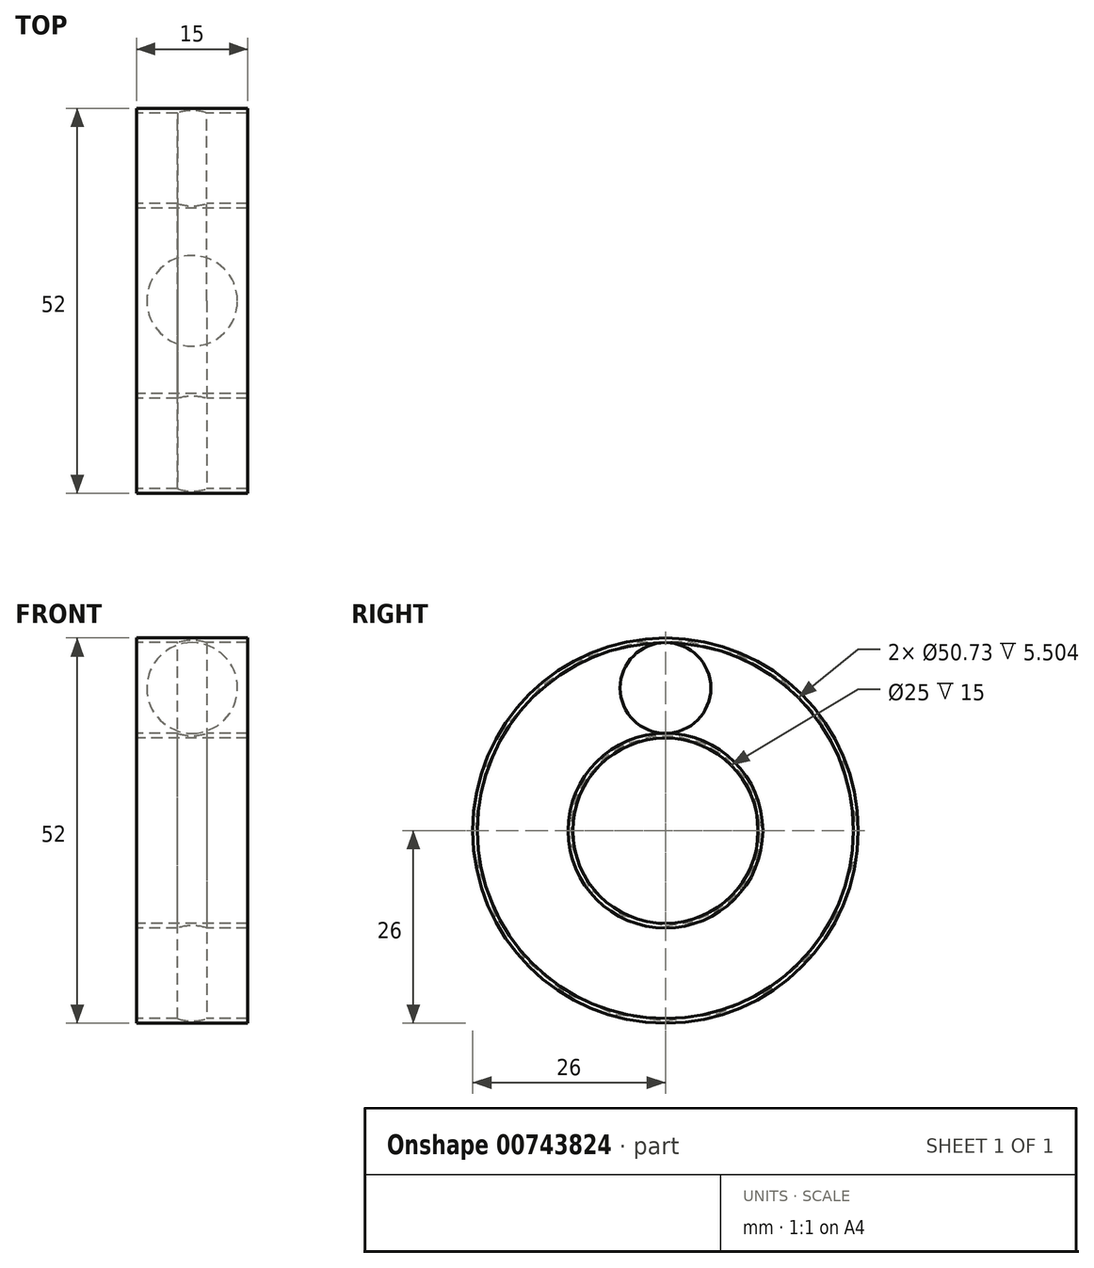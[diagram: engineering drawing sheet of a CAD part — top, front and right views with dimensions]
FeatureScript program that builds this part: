
annotation { "Feature Type Name" : "Feature", "Feature Type Description" : "" }
export const myFeature = defineFeature(function(context is Context, id is Id, definition is map)
    precondition{}
    {
        {
            var Q0;
            Q0=qCreatedBy(makeId("Right.planeOp"),FACE);
            var sketch = newSketch(context, id + "F0", { "sketchPlane" : qUnion([Q0])});
            skCircle(sketch, "E0", {"center": v(0, 0) * mm, "radius": 12.5 * mm});
            skCircle(sketch, "E1", {"center": v(0, 0) * mm, "radius": 13.14 * mm});
            skCircle(sketch, "E2", {"center": v(0, 0) * mm, "radius": 25.37 * mm});
            skCircle(sketch, "E3", {"center": v(0, 0) * mm, "radius": 26 * mm});
            skLineSegment(sketch, "E4", {"start": v(0, 13.14) * mm, "end": v(0, 19.25) * mm});
            skLineSegment(sketch, "E5", {"start": v(0, 19.25) * mm, "end": v(0, 25.37) * mm});
            skCircle(sketch, "E6", {"center": v(0, 19.25) * mm, "radius": 6.11 * mm});
            skSolve(sketch);
        }
        {
            var Q0;
            Q0=makeQuery(id+"F0.imprint","IMPRINT",FACE,{"disambiguationData":[TD([[makeQuery(id+"F0.imprint","IMPRINT",EDGE,{"derivedFrom":sQuery(id+"F0.wireOp",EDGE,"E0")}),-1.0]])]});
            var Q1;
            {var subQ0=sQuery(id+"F0.wireOp",EDGE,"E1");var subQ1=makeQuery(id+"F0.imprint","INTERSECT",VERTEX,{"derivedFrom":[subQ0,sQuery(id+"F0.wireOp",EDGE,"E4")]});Q1=makeQuery(id+"F0.imprint","IMPRINT",FACE,{"disambiguationData":[TD([[makeQuery(id+"F0.imprint","IMPRINT",EDGE,{"disambiguationData":[TD([[subQ1,1.0]])],"derivedFrom":subQ0}),1.0]])]});}
            var Q2;
            Q2=makeQuery(id+"F0.imprint","IMPRINT",FACE,{"disambiguationData":[TD([[makeQuery(id+"F0.imprint","IMPRINT",EDGE,{"derivedFrom":sQuery(id+"F0.wireOp",EDGE,"E3")}),1.0]])]});
            var Q3;
            {var subQ0=sQuery(id+"F0.wireOp",EDGE,"E2");var subQ1=makeQuery(id+"F0.imprint","INTERSECT",VERTEX,{"derivedFrom":[subQ0,sQuery(id+"F0.wireOp",EDGE,"E5")]});Q3=makeQuery(id+"F0.imprint","IMPRINT",FACE,{"disambiguationData":[TD([[makeQuery(id+"F0.imprint","IMPRINT",EDGE,{"disambiguationData":[TD([[subQ1,1.0]])],"derivedFrom":subQ0}),-1.0]])]});}
            extrude(context, id + "F1", {"entities" : qUnion([Q0, Q1, Q2, Q3]), "endBound" : BoundingType.SYMMETRIC, "depth" : 15 * mm, "offsetDistance" : 25.4 * mm});
        }
        {
            var Q0;
            Q0=qCreatedBy(makeId("Front.planeOp"),FACE);
            var sketch = newSketch(context, id + "F2", { "sketchPlane" : qUnion([Q0])});
            skPoint(sketch, "E7", {"position": v(0, 19.25) * mm});
            skCircle(sketch, "E8", {"center": v(0, 19.25) * mm, "radius": 6.43 * mm});
            skSolve(sketch);
        }
        {
            var Q0;
            Q0=makeQuery(id+"F2.imprint","IMPRINT",FACE,{"disambiguationData":[TD([[makeQuery(id+"F2.imprint","IMPRINT",EDGE,{"derivedFrom":sQuery(id+"F2.wireOp",EDGE,"E8")}),1.0]])]});
            var Q1;
            Q1=makeQuery(id+"F1.opExtrude","SWEPT_FACE",FACE,{"disambiguationData":[OSD([sQuery(id+"F0.wireOp",EDGE,"E0")])]});
            revolve(context, id + "F3", {"operationType" : NewBodyOperationType.REMOVE, "surfaceOperationType" : NewSurfaceOperationType.NEW, "entities" : qUnion([Q0]), "axis" : qUnion([Q1]), "revolveType" : RevolveType.FULL, "oppositeDirection" : true});
        }
        {
            var Q0;
            {var subQ0=sQuery(id+"F0.wireOp",EDGE,"E4");Q0=makeQuery(id+"F0.imprint","IMPRINT",FACE,{"disambiguationData":[TD([[makeQuery(id+"F0.imprint","IMPRINT",EDGE,{"derivedFrom":subQ0}),-1.0]])]});}
            var Q1;
            Q1=sQuery(id+"F0.wireOp",EDGE,"E5");
            revolve(context, id + "F4", {"surfaceOperationType" : NewSurfaceOperationType.NEW, "entities" : qUnion([Q0]), "axis" : qUnion([Q1]), "revolveType" : RevolveType.FULL});
        }
    });
